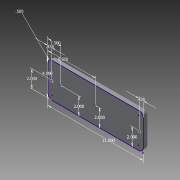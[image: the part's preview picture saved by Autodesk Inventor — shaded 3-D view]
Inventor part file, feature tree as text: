
AUTODESK INVENTOR PART (.ipt)
format: ipt  version: 2015 (Build 190159000, 159)  size: 132,608 bytes
history: native  units: in
note: dims shown in document units (in); Inventor stores cm internally (conversion verified against a paired STEP export)
features: hole x5, sketch x2, chamfer x2, extrude x1
ambient origin geometry x8: Origin, YZ Plane, XZ Plane, XY Plane, X Axis, Y Axis, Z Axis, Center Point
bodies: Solid1 (feature_tree)
feature tree (10):
  sketch  "Sketch1"  dims[d0=4.0in d1=11.0in]
  extrude  "Extrusion1"  Depth=11.0in
  hole  "Hole1"  [1 undecoded]
  hole  "Hole2"  [1 undecoded]
  hole  "Hole3"  [1 undecoded]
  hole  "Hole4"  [1 undecoded]
  chamfer  "Chamfer1"  Distance=2.0in
  chamfer  "Chamfer2"  Distance=1.5in
  hole  "Hole5"  [1 undecoded]
  sketch  "Sketch2"  dims[d2=0.5in d5=0.4375in d6=2.0in d7=2.0in d8=2.0in d9=2.0in d10=1.5in d11=5.5in d12=0.4375in d13=0.5in d14=0.0in d15=0.25in d16=0.75in d17=0.5in d18=0.25in d19=0.5635in d20=1.0in d21=0.8108in d22=0.25in d23=0.75in d24=0.5in d25=0.25in d26=0.5635in d27=1.0in d28=0.8108in d29=0.3125in d30=0.75in d31=0.5in d32=0.25in d33=0.5635in d34=1.0in d35=0.8108in d36=0.3125in d37=0.75in d38=0.5in d39=0.25in d40=0.5635in d41=1.0in d42=0.8108in d43=0.0312in d44=0.125in d45=45.0deg d46=0.0312in d47=0.125in d48=45.0deg d49=0.13in d50=0.2875in d51=0.119in d52=0.25in d53=0.5635in d54=0.2875in d55=0.0in]
note: 5 required parameter values undecoded (feature->parameter linkage not recoverable at this tier; creation-order binding heuristic only, values carry confidence <= 0.55)
